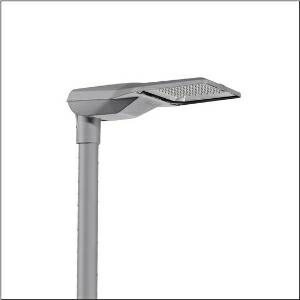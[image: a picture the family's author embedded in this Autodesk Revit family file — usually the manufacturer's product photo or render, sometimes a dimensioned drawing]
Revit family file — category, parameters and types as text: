
# Revit family: streetlight_sl_21_iq_midi___stw1_0a_5xe3e31d08mb_516a
name_source: partatom
category: Lighting Fixtures
units: mm (PartAtom-declared; Revit-internal decimal feet)

## family parameters
Cut with Voids When Loaded = No
Host = Face
Light Source = No
Part Type = Normal
Room Calculation Point = No
Round Connector Dimension = Use Diameter
Shared = No

## types (1)
- --- (1 x LED, 19500 lm, 146.7 W, 3000K)
    Apparent Load = 147 VA
    CIE Flux Codes = 38 75 98 100 100
    Color Rendering = 70
    Color Temperature = 3000K
    Default Elevation = 1800 mm
    Description = Streetlight SL 21 iQ midi, mast luminaire, primary light control with lens, of PMMA, primary optical cover: cover, of toughened safety glass, transparent, light distribution: STW1.0a, light emission: direct distribution, primary light characteristic: asymmetric, installation type: post-top, side-entry, LED, High Power LED, rated luminous flux: 19.500lm, luminous efficacy: 133lm/W, light colour: 730, colour temperature: 3000K, control gear: iQ-Comfort, control: Auto-Match, Temp-Guard, Lumen-Switch, Night-Set, Smart-Wire, Light-Fading, Desk-Remote (wireless, voltage-free reading and setting of iQ features in the workshop via application-optimized NFC function/RFID function), optimised constant luminous flux control (CLO 2.0), pre-setting: linear dimming characteristic, mains connection: 230..240V, AC, 50/60Hz, start of lifetime: 147W, end of service life: 161W, reduction: 62W, luminaire housing, of diecast aluminium, powder-coated, Siteco® metallic grey (DB 702S), corrosivity category C5 mid according to DIN EN ISO 12944, please order mast flange separately, inclination adjustable: 0°, 5°, 10°, 15°, sealing non-destructively replaceable, multi-level sealing system, length: 644mm, width: 335mm, height: 110mm, mast flange for spigot size: 42mm (side-entry): 5XC10008XM4, 60/48mm (side-entry/post-top): 5XC10108XM2, 76/60mm (side-entry/post-top): 5XC10108XM1, mounting height: 4..8m, protection rating (complete): IP66, insulation class (complete): insulation class II (safety insulation), certification: CE, ENEC, ENEC+, VDE, impact resistance: IK10, permissible operating ambient temperature for outdoor applications: -40..+50°C, standard-compliant lighting for roads and squares, packaging unit: 1 piece

Light Distribution: STW1.0a
    Height = 111 mm
    Lamp = 1 x LED
    Lamp Light Flux = 19500 lm
    Lamp Power = 146.7 W
    Lamp count = 1
    Length = 644 mm
    Luminous efficacy = 133 lm/W
    Manufacturer = Siteco
    ModVariant = No
    Model = 5XE3E31D08MB
    Number of Poles = 1
    OnlyDefault = Yes
    Power Factor = 1
    Product Name = Streetlight SL 21 iQ midi | STW1.0a
    Product group = mast luminaire | pylon top
    ProductGroupID = 6100
    Protection Class = Protection class II
    Protection Degree = IP 66
    RLX_Detail_Level = 1
    RLX_Emergency_Light_Flux = 0 lm
    RLX_Emergency_Type = 0
    RLX_Emergency_Type_DB = No
    RlxData = <blob elided: 26993 chars, md5=8993d9e8>
    Socket = socket
    Standby Power = 0 W
    System Light Flux = 19499 lm
    System Power = 147 W
    Type Comments = factory setting: luminous flux: 100 % | dim-lin: 254 | 753 mA
    Type Image = l_1004298.jpg
    URL = http://relux.com
    VarID = @adj_209437
    Voltage = 0 V
    Weight = 0.00 kg
    Width = 336 mm

## geometry (parser evidence)
native form markers: Blend x4, Sweep x9
no freeform markers — native parametric forms only
